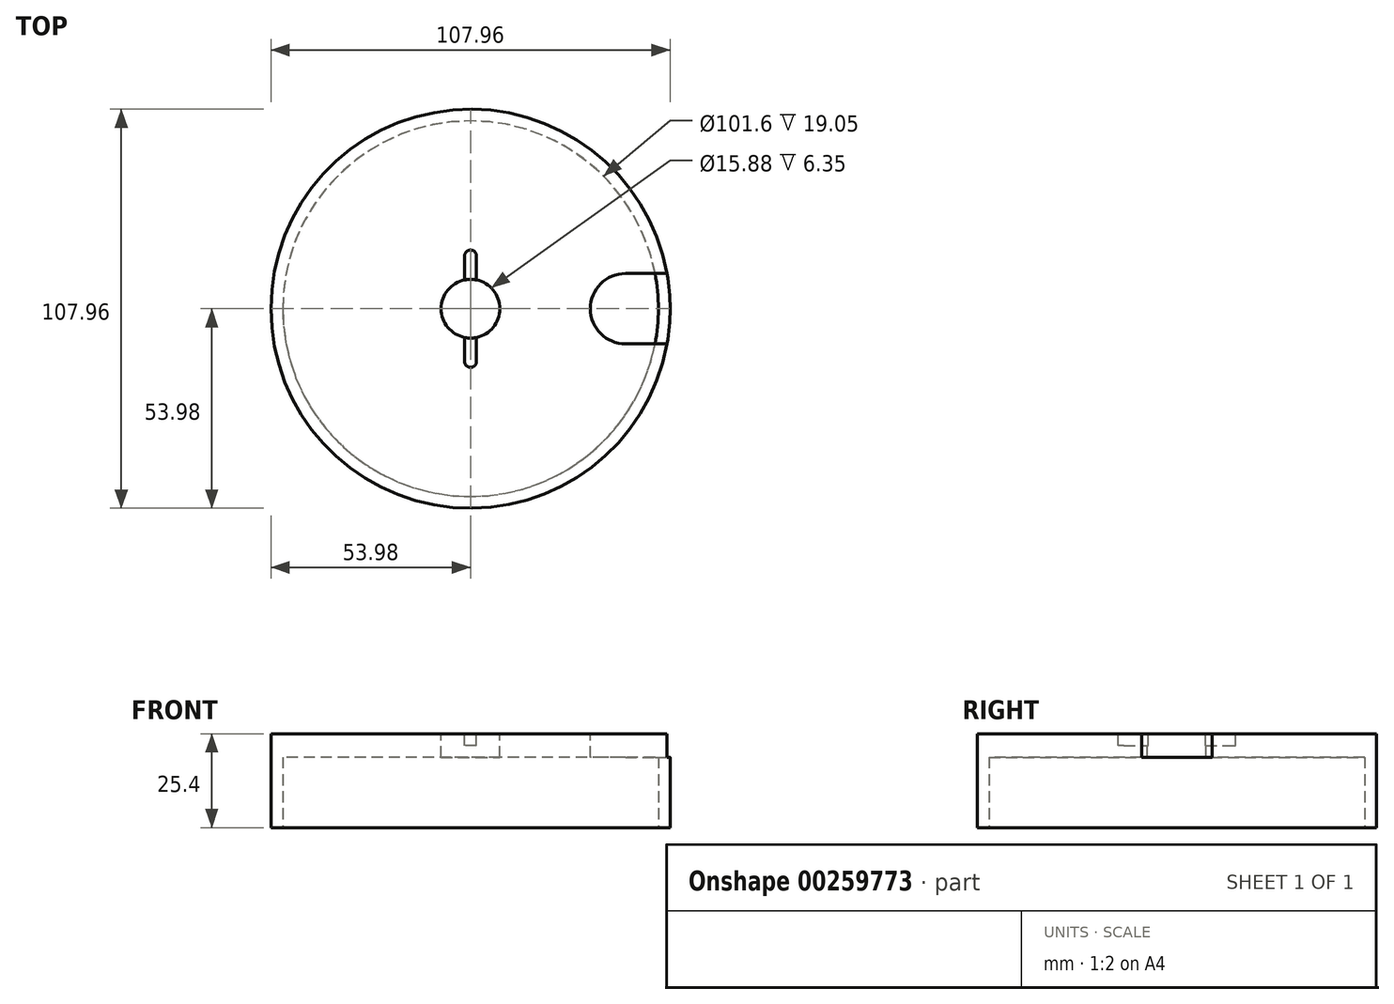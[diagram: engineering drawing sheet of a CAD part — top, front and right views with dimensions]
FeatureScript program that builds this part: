
annotation { "Feature Type Name" : "Feature", "Feature Type Description" : "" }
export const myFeature = defineFeature(function(context is Context, id is Id, definition is map)
    precondition{}
    {
        {
            var Q0;
            Q0=qCreatedBy(makeId("Top.planeOp"),FACE);
            var sketch = newSketch(context, id + "F0", { "sketchPlane" : qUnion([Q0])});
            skCircle(sketch, "E0", {"center": v(0, 0) * mm, "radius": 53.98 * mm});
            skSolve(sketch);
        }
        {
            var Q0;
            Q0=qSketchRegion(id+"F0",true);
            extrude(context, id + "F1", {"entities" : qUnion([Q0]), "depth" : 25.4 * mm});
        }
        {
            var Q0;
            Q0=makeQuery(id+"F1.opExtrude","CAP_FACE",FACE,{"disambiguationData":[OSD([sQuery(id+"F0.wireOp",EDGE,"E0")])],"isStart":true});
            var sketch = newSketch(context, id + "F2", { "sketchPlane" : qUnion([Q0])});
            skCircle(sketch, "E1", {"center": v(0, 0) * mm, "radius": 50.8 * mm});
            skSolve(sketch);
        }
        {
            var Q0;
            Q0=qSketchRegion(id+"F2",true);
            extrude(context, id + "F3", {"entities" : qUnion([Q0]), "operationType" : NewBodyOperationType.REMOVE, "oppositeDirection" : true, "depth" : 19.05 * mm});
        }
        {
            var Q0;
            Q0=makeQuery(id+"F1.opExtrude","CAP_FACE",FACE,{"disambiguationData":[OSD([sQuery(id+"F0.wireOp",EDGE,"E0")])],"isStart":false});
            var sketch = newSketch(context, id + "F4", { "sketchPlane" : qUnion([Q0])});
            skCircle(sketch, "E2", {"center": v(41.91, 0) * mm, "radius": 9.53 * mm});
            skLineSegment(sketch, "E3", {"start": v(41.91, 0) * mm, "end": v(53.98, 0) * mm, "construction": true});
            skSolve(sketch);
        }
        {
            var Q0;
            Q0=qSketchRegion(id+"F4",true);
            var Q1;
            Q1=makeQuery(id+"F3.boolean.opBoolean","COPY",FACE,{"derivedFrom":makeQuery(id+"F3.opExtrude","CAP_FACE",FACE,{"disambiguationData":[OSD([sQuery(id+"F2.wireOp",EDGE,"E1")])],"isStart":false})});
            extrude(context, id + "F5", {"entities" : qUnion([Q0]), "operationType" : NewBodyOperationType.REMOVE, "endBound" : BoundingType.UP_TO_SURFACE, "oppositeDirection" : true, "endBoundEntityFace" : qUnion([Q1]), "depth" : 6.35 * mm});
        }
        {
            var Q0;
            Q0=makeQuery(id+"F1.opExtrude","CAP_FACE",FACE,{"disambiguationData":[OSD([sQuery(id+"F0.wireOp",EDGE,"E0")])],"isStart":false});
            var sketch = newSketch(context, id + "F6", { "sketchPlane" : qUnion([Q0])});
            skLineSegment(sketch, "E4.bottom", {"start": v(41.91, 9.53) * mm, "end": v(59.03, 9.53) * mm});
            skLineSegment(sketch, "E4.top", {"start": v(41.91, -9.53) * mm, "end": v(59.03, -9.53) * mm});
            skLineSegment(sketch, "E4.left", {"start": v(41.91, 9.52) * mm, "end": v(41.91, -9.53) * mm});
            skLineSegment(sketch, "E4.right", {"start": v(59.03, 9.53) * mm, "end": v(59.03, -9.53) * mm});
            skSolve(sketch);
        }
        {
            var Q0;
            Q0=qSketchRegion(id+"F6",true);
            var Q1;
            Q1=makeQuery(id+"F3.boolean.opBoolean","COPY",FACE,{"derivedFrom":makeQuery(id+"F3.opExtrude","CAP_FACE",FACE,{"disambiguationData":[OSD([sQuery(id+"F2.wireOp",EDGE,"E1")])],"isStart":false})});
            extrude(context, id + "F7", {"entities" : qUnion([Q0]), "operationType" : NewBodyOperationType.REMOVE, "endBound" : BoundingType.UP_TO_SURFACE, "oppositeDirection" : true, "endBoundEntityFace" : qUnion([Q1]), "depth" : 25.4 * mm});
        }
        {
            var Q0;
            Q0=makeQuery(id+"F1.opExtrude","CAP_FACE",FACE,{"disambiguationData":[OSD([sQuery(id+"F0.wireOp",EDGE,"E0")])],"isStart":false});
            var sketch = newSketch(context, id + "F8", { "sketchPlane" : qUnion([Q0])});
            skCircle(sketch, "E5", {"center": v(0, 0) * mm, "radius": 7.94 * mm});
            skSolve(sketch);
        }
        {
            var Q0;
            Q0 = qSketchRegion(id + "F8", true);
            var Q1;
            Q1=makeQuery(id+"F3.boolean.opBoolean","COPY",FACE,{"derivedFrom":makeQuery(id+"F3.opExtrude","CAP_FACE",FACE,{"disambiguationData":[OSD([sQuery(id+"F2.wireOp",EDGE,"E1")])],"isStart":false})});
            extrude(context, id + "F9", {"entities" : qUnion([Q0]), "operationType" : NewBodyOperationType.REMOVE, "endBound" : BoundingType.UP_TO_SURFACE, "oppositeDirection" : true, "endBoundEntityFace" : qUnion([Q1]), "depth" : 25.4 * mm});
        }
        {
            var Q0;
            Q0=makeQuery(id+"F1.opExtrude","CAP_FACE",FACE,{"disambiguationData":[OSD([sQuery(id+"F0.wireOp",EDGE,"E0")])],"isStart":false});
            var sketch = newSketch(context, id + "F10", { "sketchPlane" : qUnion([Q0])});
            skLineSegment(sketch, "E6.bottom", {"start": v(0, -15.88) * mm, "end": v(0, -15.88) * mm});
            skLineSegment(sketch, "E6.top", {"start": v(0, 15.88) * mm, "end": v(0, 15.88) * mm});
            skLineSegment(sketch, "E6.left", {"start": v(1.59, -14.29) * mm, "end": v(1.59, 14.29) * mm});
            skLineSegment(sketch, "E6.right", {"start": v(-1.59, -14.29) * mm, "end": v(-1.59, 14.29) * mm});
            skPoint(sketch, "E6.middle", {"position": v(0, 0) * mm});
            skPoint(sketch, "E7.visualSharp", {"position": v(-1.59, 15.88) * mm});
            skArc(sketch, "E7.filletArc", {"start": v(0, 15.88) * mm, "mid": v(-1.12, 15.41) * mm, "end": v(-1.59, 14.29) * mm});
            skPoint(sketch, "E8.visualSharp", {"position": v(1.59, 15.88) * mm});
            skArc(sketch, "E8.filletArc", {"start": v(1.59, 14.29) * mm, "mid": v(1.12, 15.41) * mm, "end": v(0, 15.88) * mm});
            skPoint(sketch, "E9.visualSharp", {"position": v(1.59, -15.88) * mm});
            skArc(sketch, "E9.filletArc", {"start": v(0, -15.88) * mm, "mid": v(1.12, -15.41) * mm, "end": v(1.59, -14.29) * mm});
            skPoint(sketch, "E10.visualSharp", {"position": v(-1.59, -15.88) * mm});
            skArc(sketch, "E10.filletArc", {"start": v(-1.59, -14.29) * mm, "mid": v(-1.12, -15.41) * mm, "end": v(0, -15.88) * mm});
            skSolve(sketch);
        }
        {
            var Q0;
            Q0 = qSketchRegion(id + "F10", true);
            extrude(context, id + "F11", {"entities" : qUnion([Q0]), "operationType" : NewBodyOperationType.REMOVE, "oppositeDirection" : true, "depth" : 3.17 * mm});
        }
    });
